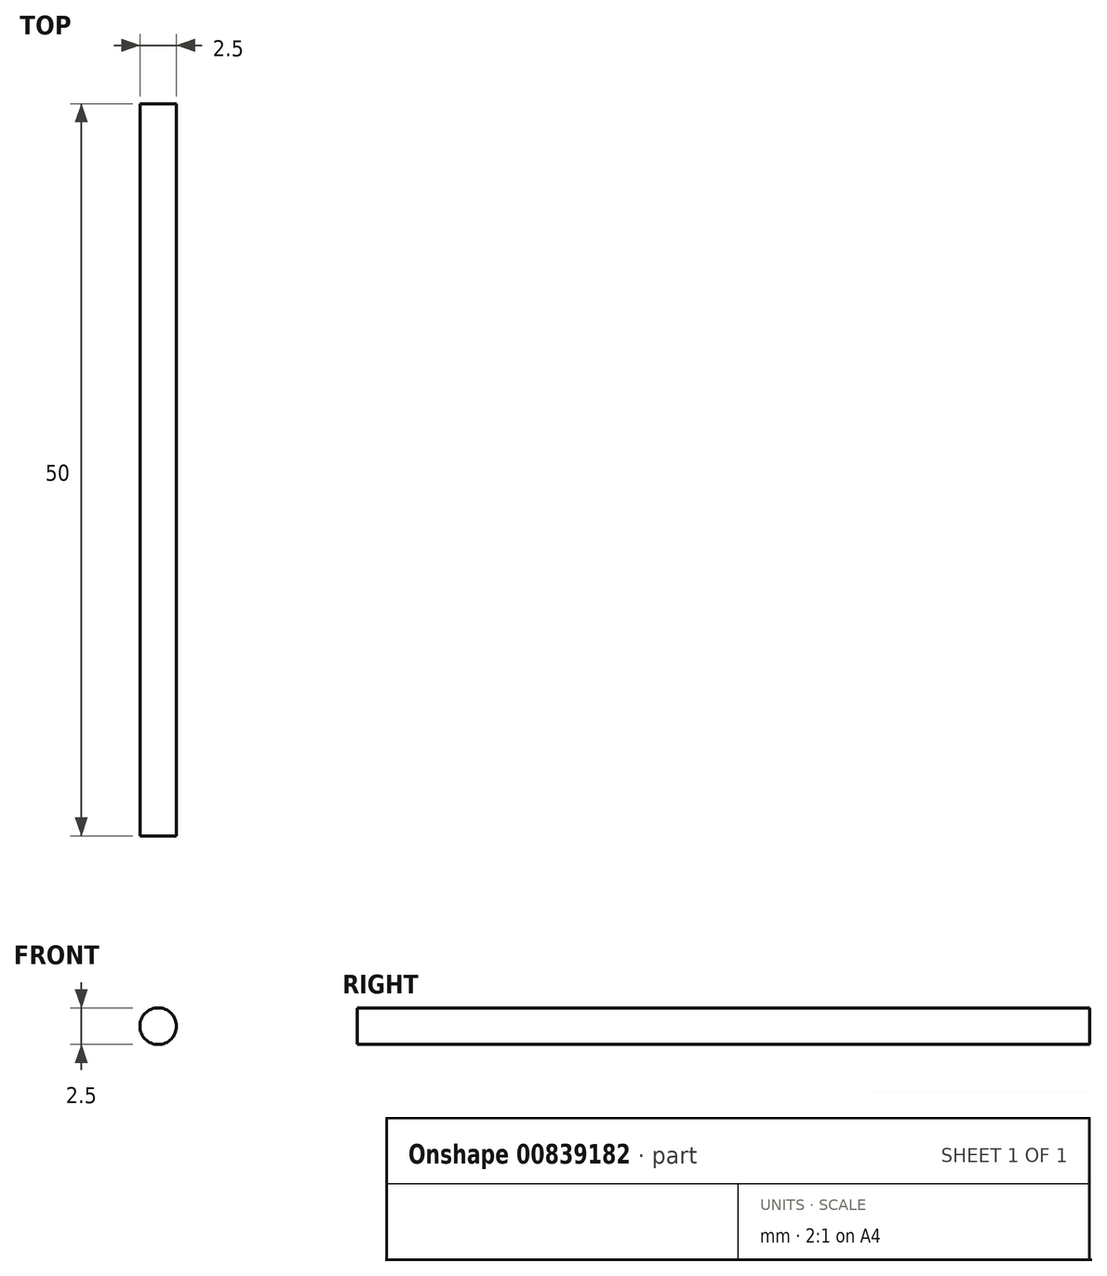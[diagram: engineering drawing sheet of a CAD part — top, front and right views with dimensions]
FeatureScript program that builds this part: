
annotation { "Feature Type Name" : "Feature", "Feature Type Description" : "" }
export const myFeature = defineFeature(function(context is Context, id is Id, definition is map)
    precondition{}
    {
        {
            var Q0;
            Q0=qCreatedBy(makeId("Front.planeOp"),FACE);
            var sketch = newSketch(context, id + "F0", { "sketchPlane" : qUnion([Q0])});
            skCircle(sketch, "E0", {"center": v(0, 0) * mm, "radius": 1.25 * mm});
            skSolve(sketch);
        }
        {
            var Q0;
            Q0=makeQuery(id+"F0.imprint","IMPRINT",FACE,{"disambiguationData":[TD([[makeQuery(id+"F0.imprint","IMPRINT",EDGE,{"derivedFrom":sQuery(id+"F0.wireOp",EDGE,"E0")}),1.0]])]});
            extrude(context, id + "F1", {"entities" : qUnion([Q0]), "depth" : 50 * mm, "offsetDistance" : 25 * mm});
        }
    });
